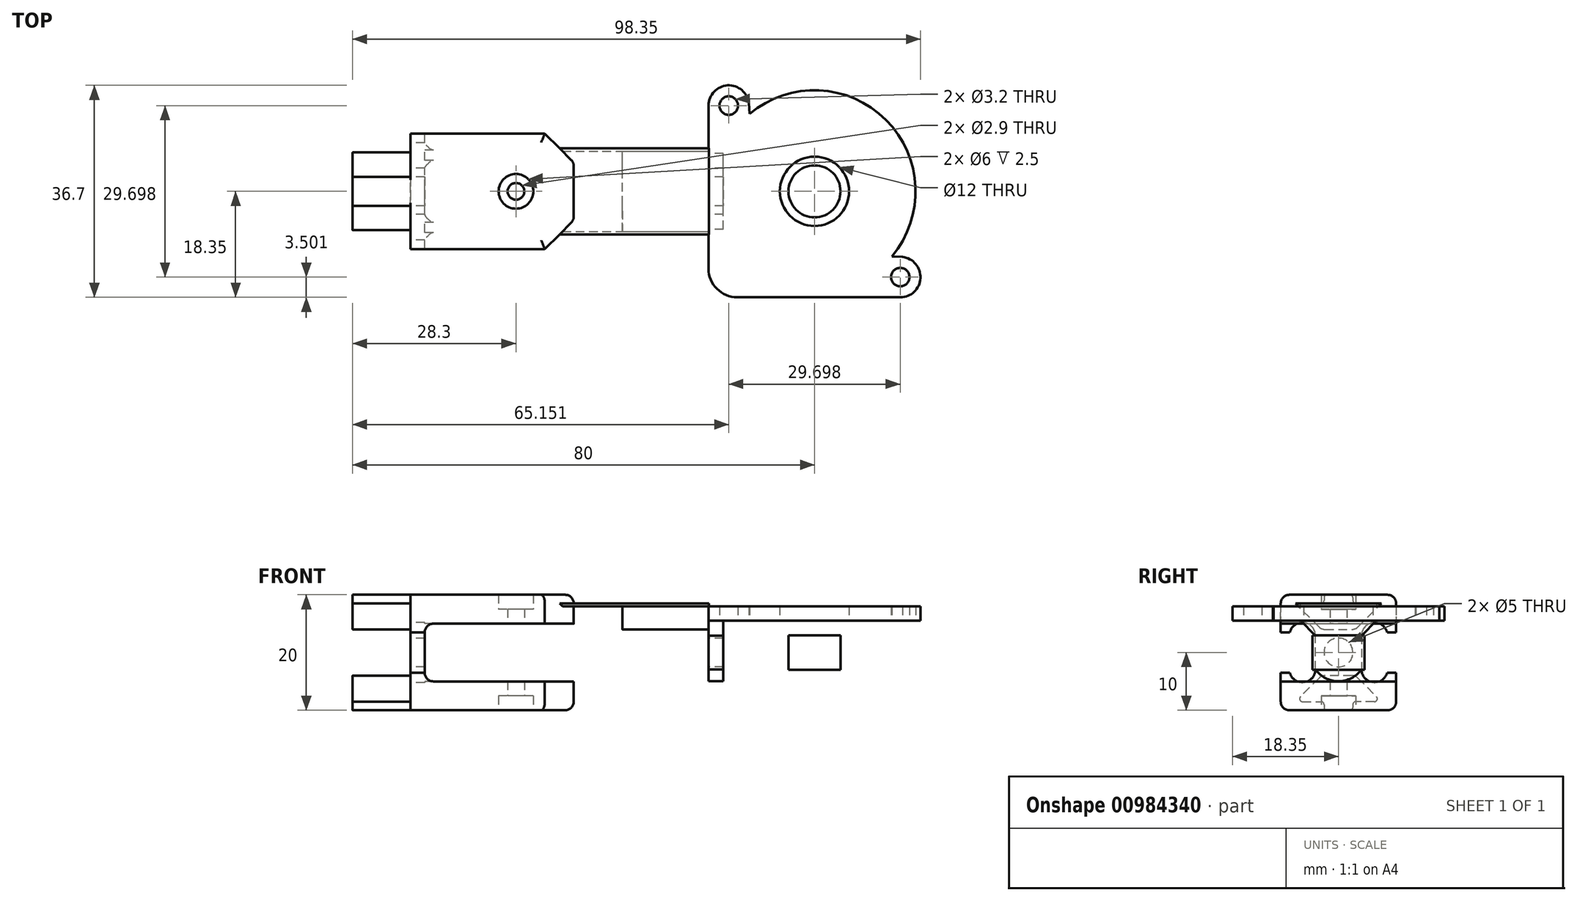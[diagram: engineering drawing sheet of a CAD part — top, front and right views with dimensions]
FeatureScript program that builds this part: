
annotation { "Feature Type Name" : "Feature", "Feature Type Description" : "" }
export const myFeature = defineFeature(function(context is Context, id is Id, definition is map)
    precondition{}
    {
        {
            var Q0;
            Q0=qCreatedBy(makeId("Top.planeOp"),FACE);
            cPlane(context, id + "F0", {"entities" : qUnion([Q0]), "cplaneType" : CPlaneType.OFFSET, "offset" : 2.5 * mm, "oppositeDirection" : true, "width" : 150 * mm, "height" : 150 * mm});
        }
        {
            var Q0;
            Q0=qCreatedBy(makeId("Right.planeOp"),FACE);
            cPlane(context, id + "F1", {"entities" : qUnion([Q0]), "cplaneType" : CPlaneType.OFFSET, "offset" : 18.3 * mm, "oppositeDirection" : true, "width" : 150 * mm, "height" : 150 * mm});
        }
        {
            var Q0;
            Q0=qCreatedBy(makeId("Right.planeOp"),FACE);
            cPlane(context, id + "F2", {"entities" : qUnion([Q0]), "cplaneType" : CPlaneType.OFFSET, "offset" : 70 * mm, "oppositeDirection" : true, "width" : 150 * mm, "height" : 150 * mm});
        }
        {
            var Q0;
            Q0=qCreatedBy(makeId("Top.planeOp"),FACE);
            cPlane(context, id + "F3", {"entities" : qUnion([Q0]), "cplaneType" : CPlaneType.OFFSET, "offset" : 5.5 * mm, "oppositeDirection" : true, "width" : 150 * mm, "height" : 150 * mm});
        }
        {
            var Q0;
            Q0=qCreatedBy(makeId("Top.planeOp"),FACE);
            var sketch = newSketch(context, id + "F4", { "sketchPlane" : qUnion([Q0])});
            skLineSegment(sketch, "E0", {"start": v(-14.85, 14.85) * mm, "end": v(14.85, -14.85) * mm, "construction": true});
            skCircle(sketch, "E1", {"center": v(14.85, -14.85) * mm, "radius": 1.6 * mm});
            skCircle(sketch, "E2", {"center": v(0, 0) * mm, "radius": 6 * mm});
            skCircle(sketch, "E3", {"center": v(-14.85, 14.85) * mm, "radius": 1.6 * mm});
            skLineSegment(sketch, "E4", {"start": v(-18.35, 14.85) * mm, "end": v(-17.47, -0.97) * mm, "construction": true});
            skLineSegment(sketch, "E5", {"start": v(-0.97, -17.47) * mm, "end": v(14.85, -18.35) * mm, "construction": true});
            skLineSegment(sketch, "E6", {"start": v(-11.26, 13.4) * mm, "end": v(-11.37, 15.24) * mm});
            skLineSegment(sketch, "E7", {"start": v(13.4, -11.26) * mm, "end": v(15.24, -11.37) * mm});
            skArc(sketch, "E8", {"start": v(-18.35, 14.85) * mm, "mid": v(-15.04, 18.35) * mm, "end": v(-11.37, 15.24) * mm});
            skArc(sketch, "E9", {"start": v(15.24, -11.37) * mm, "mid": v(18.35, -15.04) * mm, "end": v(14.85, -18.35) * mm});
            skArc(sketch, "E10", {"start": v(-17.47, -0.97) * mm, "mid": v(-12.37, -12.37) * mm, "end": v(-0.97, -17.47) * mm, "construction": true});
            skArc(sketch, "E11", {"start": v(-11.26, 13.4) * mm, "mid": v(12.37, 12.37) * mm, "end": v(13.4, -11.26) * mm});
            skLineSegment(sketch, "E12.0", {"start": v(-18.35, 14.85) * mm, "end": v(14.85, -18.35) * mm, "construction": true});
            skLineSegment(sketch, "E13.top", {"start": v(-18.35, -18.35) * mm, "end": v(14.85, -18.35) * mm});
            skLineSegment(sketch, "E13.left", {"start": v(-18.35, 14.85) * mm, "end": v(-18.35, -18.35) * mm});
            skLineSegment(sketch, "E14", {"start": v(-40.55, 25) * mm, "end": v(-40.55, -27.36) * mm, "construction": true});
            skLineSegment(sketch, "E15.MirrorCS", {"start": v(-94.5, -11.26) * mm, "end": v(-96.35, -11.37) * mm});
            skLineSegment(sketch, "E16.MirrorCS", {"start": v(-69.84, 13.4) * mm, "end": v(-69.74, 15.24) * mm});
            skArc(sketch, "E17.MirrorCS", {"start": v(-62.75, 14.85) * mm, "mid": v(-66.06, 18.35) * mm, "end": v(-69.74, 15.24) * mm});
            skArc(sketch, "E18.MirrorCS", {"start": v(-69.84, 13.4) * mm, "mid": v(-93.48, 12.37) * mm, "end": v(-94.5, -11.26) * mm});
            skCircle(sketch, "E19.MirrorC", {"center": v(-95.96, -14.85) * mm, "radius": 1.6 * mm});
            skLineSegment(sketch, "E20.MirrorCS", {"start": v(-62.75, -18.35) * mm, "end": v(-95.96, -18.35) * mm});
            skCircle(sketch, "E21.MirrorC", {"center": v(-66.26, 14.85) * mm, "radius": 1.6 * mm});
            skArc(sketch, "E22.MirrorCS", {"start": v(-96.35, -11.37) * mm, "mid": v(-99.46, -15.04) * mm, "end": v(-95.96, -18.35) * mm});
            skLineSegment(sketch, "E23.MirrorCS", {"start": v(-62.75, 14.85) * mm, "end": v(-62.75, -18.35) * mm});
            skCircle(sketch, "E24", {"center": v(-81.1, 0) * mm, "radius": 1.35 * mm});
            skSolve(sketch);
        }
        {
            var Q0;
            Q0=qCreatedBy(id+"F0.planeOp",FACE);
            var sketch = newSketch(context, id + "F5", { "sketchPlane" : qUnion([Q0])});
            skCircle(sketch, "E25", {"center": v(0, 0) * mm, "radius": 4.5 * mm});
            skSolve(sketch);
        }
        {
            var Q0;
            Q0=qCreatedBy(id+"F1.planeOp",FACE);
            var sketch = newSketch(context, id + "F6", { "sketchPlane" : qUnion([Q0])});
            skLineSegment(sketch, "E26.0", {"start": v(4, -2.56) * mm, "end": v(6.56, 0) * mm});
            skLineSegment(sketch, "E26.1", {"start": v(4, -2.56) * mm, "end": v(4, -8.44) * mm});
            skLineSegment(sketch, "E26.2", {"start": v(-4, -8.44) * mm, "end": v(-4, -2.56) * mm});
            skLineSegment(sketch, "E26.3", {"start": v(-6.56, 0) * mm, "end": v(-4, -2.56) * mm});
            skCircle(sketch, "E26.4", {"center": v(0, -5.5) * mm, "radius": 2.5 * mm});
            skCircle(sketch, "E27", {"center": v(0, 0) * mm, "radius": 2.5 * mm, "construction": true});
            skArc(sketch, "E28", {"start": v(-4, -8.44) * mm, "mid": v(0, -10.46) * mm, "end": v(4, -8.44) * mm});
            skLineSegment(sketch, "E29", {"start": v(-2.94, -1.5) * mm, "end": v(2.94, -1.5) * mm});
            skLineSegment(sketch, "E30", {"start": v(-6.56, 0) * mm, "end": v(-6.94, 2.5) * mm});
            skLineSegment(sketch, "E31", {"start": v(6.56, 0) * mm, "end": v(6.94, 2.5) * mm});
            skLineSegment(sketch, "E32", {"start": v(-6.94, 2.5) * mm, "end": v(6.94, 2.5) * mm});
            skLineSegment(sketch, "E33", {"start": v(-2.94, -1.5) * mm, "end": v(-6.94, 2.5) * mm});
            skLineSegment(sketch, "E34", {"start": v(2.94, -1.5) * mm, "end": v(6.94, 2.5) * mm});
            skLineSegment(sketch, "E35", {"start": v(-7.44, 3) * mm, "end": v(7.44, 3) * mm});
            skLineSegment(sketch, "E36", {"start": v(-7.44, 3) * mm, "end": v(-6.94, 2.5) * mm});
            skLineSegment(sketch, "E37", {"start": v(7.44, 3) * mm, "end": v(6.94, 2.5) * mm});
            skSolve(sketch);
        }
        {
            var Q0;
            Q0=qCreatedBy(id+"F2.planeOp",FACE);
            var sketch = newSketch(context, id + "F7", { "sketchPlane" : qUnion([Q0])});
            skCircle(sketch, "E38.0", {"center": v(0, -5.5) * mm, "radius": 2.5 * mm});
            skLineSegment(sketch, "E39", {"start": v(-2.5, -14) * mm, "end": v(-2.5, -15.5) * mm});
            skLineSegment(sketch, "E40", {"start": v(-10, -9) * mm, "end": v(-8.43, -9) * mm});
            skLineSegment(sketch, "E41", {"start": v(-10, -2) * mm, "end": v(-8.43, -2) * mm});
            skLineSegment(sketch, "E42", {"start": v(2.5, -14) * mm, "end": v(2.5, -15.5) * mm});
            skLineSegment(sketch, "E43", {"start": v(8.43, -9) * mm, "end": v(10, -9) * mm});
            skLineSegment(sketch, "E44", {"start": v(8.43, -2) * mm, "end": v(10, -2) * mm});
            skLineSegment(sketch, "E45", {"start": v(-2.94, -1.5) * mm, "end": v(-7.44, 3) * mm});
            skLineSegment(sketch, "E46", {"start": v(2.94, -1.5) * mm, "end": v(7.44, 3) * mm});
            skLineSegment(sketch, "E47", {"start": v(2.94, -9.5) * mm, "end": v(7.44, -14) * mm});
            skLineSegment(sketch, "E48", {"start": v(-2.94, -9.5) * mm, "end": v(-7.44, -14) * mm});
            skLineSegment(sketch, "E49", {"start": v(-2.5, 4.5) * mm, "end": v(-2.5, 3) * mm});
            skLineSegment(sketch, "E50", {"start": v(2.5, 4.5) * mm, "end": v(2.5, 3) * mm});
            skLineSegment(sketch, "E51", {"start": v(-7.44, -14) * mm, "end": v(-2.5, -14) * mm});
            skLineSegment(sketch, "E52", {"start": v(-2.5, 3) * mm, "end": v(-7.44, 3) * mm});
            skLineSegment(sketch, "E53", {"start": v(2.5, 3) * mm, "end": v(7.44, 3) * mm});
            skLineSegment(sketch, "E54", {"start": v(7.44, -14) * mm, "end": v(2.5, -14) * mm});
            skLineSegment(sketch, "E55", {"start": v(-2.94, -1.5) * mm, "end": v(2.94, -1.5) * mm});
            skLineSegment(sketch, "E56", {"start": v(4, -2.56) * mm, "end": v(4, -8.44) * mm});
            skLineSegment(sketch, "E57", {"start": v(2.94, -9.5) * mm, "end": v(-2.94, -9.5) * mm});
            skLineSegment(sketch, "E58", {"start": v(-4, -8.44) * mm, "end": v(-4, -2.56) * mm});
            skLineSegment(sketch, "E59", {"start": v(10, 4.5) * mm, "end": v(-10, 4.5) * mm});
            skLineSegment(sketch, "E60", {"start": v(10, 4.5) * mm, "end": v(10, -15.5) * mm});
            skLineSegment(sketch, "E61", {"start": v(-10, 4.5) * mm, "end": v(-10, -15.5) * mm});
            skLineSegment(sketch, "E62", {"start": v(10, -15.5) * mm, "end": v(-10, -15.5) * mm});
            skLineSegment(sketch, "E63", {"start": v(10, -5.5) * mm, "end": v(-10, -5.5) * mm, "construction": true});
            skLineSegment(sketch, "E64", {"start": v(0, 4.5) * mm, "end": v(0, -15.5) * mm, "construction": true});
            skArc(sketch, "E65", {"start": v(8.43, -2) * mm, "mid": v(5.97, -0.33) * mm, "end": v(4, -2.56) * mm});
            skArc(sketch, "E66", {"start": v(-8.43, -2) * mm, "mid": v(-5.97, -0.33) * mm, "end": v(-4, -2.56) * mm});
            skArc(sketch, "E67", {"start": v(-8.43, -9) * mm, "mid": v(-5.97, -10.67) * mm, "end": v(-4, -8.44) * mm});
            skArc(sketch, "E68", {"start": v(8.43, -9) * mm, "mid": v(5.97, -10.67) * mm, "end": v(4, -8.44) * mm});
            skSolve(sketch);
        }
        {
            var Q0;
            Q0=qCreatedBy(id+"F3.planeOp",FACE);
            var sketch = newSketch(context, id + "F8", { "sketchPlane" : qUnion([Q0])});
            skLineSegment(sketch, "E69.1", {"start": v(-67.5, -10) * mm, "end": v(-67.5, 10) * mm});
            skLineSegment(sketch, "E70", {"start": v(-41.7, -10) * mm, "end": v(-41.7, 10) * mm});
            skLineSegment(sketch, "E71", {"start": v(-67.5, -10) * mm, "end": v(-41.7, -10) * mm});
            skLineSegment(sketch, "E72", {"start": v(-67.5, 10) * mm, "end": v(-41.7, 10) * mm});
            skCircle(sketch, "E73", {"center": v(-51.7, 0) * mm, "radius": 1.45 * mm});
            skCircle(sketch, "E74", {"center": v(-51.7, 0) * mm, "radius": 5 * mm, "construction": true});
            skCircle(sketch, "E75", {"center": v(-51.7, 0) * mm, "radius": 3 * mm});
            skSolve(sketch);
        }
        {
            var Q0;
            Q0=makeQuery(id+"F4.imprint","IMPRINT",FACE,{"disambiguationData":[TD([[makeQuery(id+"F4.imprint","IMPRINT",EDGE,{"derivedFrom":sQuery(id+"F4.wireOp",EDGE,"E1")}),-1.0]])]});
            extrude(context, id + "F9", {"entities" : qUnion([Q0]), "depth" : 2.5 * mm, "offsetDistance" : 25 * mm});
        }
        {
            var Q0;
            Q0=makeQuery(id+"F5.imprint","IMPRINT",FACE,{"disambiguationData":[TD([[makeQuery(id+"F5.imprint","IMPRINT",EDGE,{"derivedFrom":sQuery(id+"F5.wireOp",EDGE,"E25")}),1.0]])]});
            extrude(context, id + "F10", {"entities" : qUnion([Q0]), "oppositeDirection" : true, "depth" : 6 * mm, "offsetDistance" : 25 * mm});
        }
        {
            var Q0;
            Q0=makeQuery(id+"F6.imprint","IMPRINT",FACE,{"disambiguationData":[TD([[makeQuery(id+"F6.imprint","IMPRINT",EDGE,{"derivedFrom":sQuery(id+"F6.wireOp",EDGE,"E26.0")}),1.0]])]});
            var Q1;
            Q1=makeQuery(id+"F6.imprint","IMPRINT",FACE,{"disambiguationData":[TD([[makeQuery(id+"F6.imprint","IMPRINT",EDGE,{"derivedFrom":sQuery(id+"F6.wireOp",EDGE,"E29")}),1.0]])]});
            extrude(context, id + "F11", {"entities" : qUnion([Q0, Q1]), "operationType" : NewBodyOperationType.ADD, "depth" : 2.5 * mm, "offsetDistance" : 25 * mm});
        }
        {
            var Q0;
            Q0=makeQuery(id+"F6.imprint","IMPRINT",FACE,{"disambiguationData":[TD([[makeQuery(id+"F6.imprint","IMPRINT",EDGE,{"derivedFrom":sQuery(id+"F6.wireOp",EDGE,"E26.0")}),1.0]])]});
            var Q1;
            Q1=makeQuery(id+"F6.imprint","IMPRINT",FACE,{"disambiguationData":[TD([[makeQuery(id+"F6.imprint","IMPRINT",EDGE,{"derivedFrom":sQuery(id+"F6.wireOp",EDGE,"E29")}),1.0]])]});
            extrude(context, id + "F12", {"entities" : qUnion([Q0, Q1]), "operationType" : NewBodyOperationType.ADD, "oppositeDirection" : true, "depth" : 0.2 * mm, "offsetDistance" : 25 * mm});
        }
        {
            var Q0;
            Q0=makeQuery(id+"F6.imprint","IMPRINT",FACE,{"disambiguationData":[TD([[makeQuery(id+"F6.imprint","IMPRINT",EDGE,{"derivedFrom":sQuery(id+"F6.wireOp",EDGE,"E29")}),1.0]])]});
            extrude(context, id + "F13", {"entities" : qUnion([Q0]), "operationType" : NewBodyOperationType.ADD, "oppositeDirection" : true, "depth" : 15 * mm, "offsetDistance" : 25 * mm});
        }
        {
            var Q0;
            Q0=makeQuery(id+"F12.opExtrude","CAP_FACE",FACE,{"disambiguationData":[OSD([sQuery(id+"F6.wireOp",EDGE,"E26.0"),sQuery(id+"F6.wireOp",EDGE,"E26.1"),sQuery(id+"F6.wireOp",EDGE,"E26.2"),sQuery(id+"F6.wireOp",EDGE,"E26.3"),sQuery(id+"F6.wireOp",EDGE,"E26.4"),sQuery(id+"F6.wireOp",EDGE,"E28"),sQuery(id+"F6.wireOp",EDGE,"E30"),sQuery(id+"F6.wireOp",EDGE,"E31"),sQuery(id+"F6.wireOp",EDGE,"E32")])],"isStart":false});
            var Q1;
            {var subQ0=sQuery(id+"F4.wireOp",EDGE,"E13.top");var subQ2=sQuery(id+"F4.wireOp",EDGE,"E13.left");Q1=makeQuery(id+"F12.boolean.opBoolean","SPLIT",FACE,{"disambiguationData":[TD([makeQuery(id+"F9.opExtrude","SWEPT_FACE",FACE,{"disambiguationData":[OSD([subQ0])]})])],"derivedFrom":makeQuery(id+"F9.opExtrude","SWEPT_FACE",FACE,{"disambiguationData":[OSD([subQ2])]})});}
            extrude(context, id + "F14", {"entities" : qUnion([Q0]), "operationType" : NewBodyOperationType.REMOVE, "endBound" : BoundingType.UP_TO_SURFACE, "oppositeDirection" : true, "depth" : 25 * mm, "endBoundEntityFace" : qUnion([Q1]), "offsetDistance" : 25 * mm});
        }
        {
            var Q0;
            Q0=makeQuery(id+"F6.imprint","IMPRINT",FACE,{"disambiguationData":[TD([[makeQuery(id+"F6.imprint","IMPRINT",EDGE,{"derivedFrom":sQuery(id+"F6.wireOp",EDGE,"E32")}),1.0]])]});
            extrude(context, id + "F15", {"entities" : qUnion([Q0]), "oppositeDirection" : true, "depth" : 25 * mm, "offsetDistance" : 25 * mm});
        }
        {
            var Q0;
            Q0=makeQuery(id+"F7.imprint","IMPRINT",FACE,{"disambiguationData":[TD([[makeQuery(id+"F7.imprint","IMPRINT",EDGE,{"derivedFrom":sQuery(id+"F7.wireOp",EDGE,"E38.0")}),-1.0]])]});
            var Q1;
            Q1=makeQuery(id+"F7.imprint","IMPRINT",FACE,{"disambiguationData":[TD([[makeQuery(id+"F7.imprint","IMPRINT",EDGE,{"derivedFrom":sQuery(id+"F7.wireOp",EDGE,"E45")}),-1.0]])]});
            var Q2;
            {var subQ1=sQuery(id+"F7.wireOp",EDGE,"E39");Q2=makeQuery(id+"F7.imprint","IMPRINT",FACE,{"disambiguationData":[TD([[makeQuery(id+"F7.imprint","IMPRINT",EDGE,{"derivedFrom":subQ1}),1.0]])]});}
            extrude(context, id + "F16", {"entities" : qUnion([Q0, Q1, Q2]), "depth" : 2.5 * mm, "offsetDistance" : 25 * mm});
        }
        {
            var Q0;
            Q0=makeQuery(id+"F7.imprint","IMPRINT",FACE,{"disambiguationData":[TD([[makeQuery(id+"F7.imprint","IMPRINT",EDGE,{"derivedFrom":sQuery(id+"F7.wireOp",EDGE,"E45")}),-1.0]])]});
            var Q1;
            {var subQ1=sQuery(id+"F7.wireOp",EDGE,"E39");Q1=makeQuery(id+"F7.imprint","IMPRINT",FACE,{"disambiguationData":[TD([[makeQuery(id+"F7.imprint","IMPRINT",EDGE,{"derivedFrom":subQ1}),1.0]])]});}
            extrude(context, id + "F17", {"entities" : qUnion([Q0, Q1]), "operationType" : NewBodyOperationType.ADD, "oppositeDirection" : true, "depth" : 10 * mm, "offsetDistance" : 25 * mm});
        }
        {
            var Q0;
            Q0=makeQuery(id+"F8.imprint","IMPRINT",FACE,{"disambiguationData":[TD([[makeQuery(id+"F8.imprint","IMPRINT",EDGE,{"derivedFrom":sQuery(id+"F8.wireOp",EDGE,"E69.1")}),-1.0]])]});
            extrude(context, id + "F18", {"entities" : qUnion([Q0]), "operationType" : NewBodyOperationType.ADD, "depth" : 20 * mm, "offsetDistance" : 25 * mm, "symmetric" : true});
        }
        {
            var Q0;
            Q0=makeQuery(id+"F8.imprint","IMPRINT",FACE,{"disambiguationData":[TD([[makeQuery(id+"F8.imprint","IMPRINT",EDGE,{"derivedFrom":sQuery(id+"F8.wireOp",EDGE,"E73")}),-1.0]])]});
            extrude(context, id + "F19", {"entities" : qUnion([Q0]), "operationType" : NewBodyOperationType.ADD, "depth" : 15 * mm, "offsetDistance" : 25 * mm, "symmetric" : true});
        }
        {
            var Q0;
            Q0=makeQuery(id+"F8.imprint","IMPRINT",FACE,{"disambiguationData":[TD([[makeQuery(id+"F8.imprint","IMPRINT",EDGE,{"derivedFrom":sQuery(id+"F8.wireOp",EDGE,"E69.1")}),-1.0]])]});
            var Q1;
            Q1=makeQuery(id+"F8.imprint","IMPRINT",FACE,{"disambiguationData":[TD([[makeQuery(id+"F8.imprint","IMPRINT",EDGE,{"derivedFrom":sQuery(id+"F8.wireOp",EDGE,"E73")}),-1.0]])]});
            extrude(context, id + "F20", {"entities" : qUnion([Q0, Q1]), "operationType" : NewBodyOperationType.REMOVE, "depth" : 10 * mm, "offsetDistance" : 25 * mm, "symmetric" : true});
        }
        {
            var Q0;
            {var subQ0=sQuery(id+"F7.wireOp",EDGE,"E62");var subQ3=sQuery(id+"F8.wireOp",EDGE,"E71");var subQ4=sQuery(id+"F8.wireOp",EDGE,"E70");Q0=makeQuery(id+"F20.boolean.opBoolean","SPLIT",EDGE,{"disambiguationData":[TD([makeQuery(id+"F16.opExtrude","SWEPT_FACE",FACE,{"disambiguationData":[OSD([subQ0])]})])],"derivedFrom":makeQuery(id+"F18.opExtrude","SWEPT_EDGE",EDGE,{"disambiguationData":[OSD([subQ4,subQ3])]})});}
            var Q1;
            {var subQ0=sQuery(id+"F7.wireOp",EDGE,"E62");var subQ2=sQuery(id+"F8.wireOp",EDGE,"E72");var subQ4=sQuery(id+"F8.wireOp",EDGE,"E70");Q1=makeQuery(id+"F20.boolean.opBoolean","SPLIT",EDGE,{"disambiguationData":[TD([makeQuery(id+"F16.opExtrude","SWEPT_FACE",FACE,{"disambiguationData":[OSD([subQ0])]})])],"derivedFrom":makeQuery(id+"F18.opExtrude","SWEPT_EDGE",EDGE,{"disambiguationData":[OSD([subQ4,subQ2])]})});}
            var Q2;
            {var subQ1=sQuery(id+"F7.wireOp",EDGE,"E59");var subQ3=sQuery(id+"F8.wireOp",EDGE,"E71");var subQ4=sQuery(id+"F8.wireOp",EDGE,"E70");Q2=makeQuery(id+"F20.boolean.opBoolean","SPLIT",EDGE,{"disambiguationData":[TD([makeQuery(id+"F16.opExtrude","SWEPT_FACE",FACE,{"disambiguationData":[OSD([subQ1])]})])],"derivedFrom":makeQuery(id+"F18.opExtrude","SWEPT_EDGE",EDGE,{"disambiguationData":[OSD([subQ4,subQ3])]})});}
            var Q3;
            {var subQ1=sQuery(id+"F7.wireOp",EDGE,"E59");var subQ2=sQuery(id+"F8.wireOp",EDGE,"E72");var subQ4=sQuery(id+"F8.wireOp",EDGE,"E70");Q3=makeQuery(id+"F20.boolean.opBoolean","SPLIT",EDGE,{"disambiguationData":[TD([makeQuery(id+"F16.opExtrude","SWEPT_FACE",FACE,{"disambiguationData":[OSD([subQ1])]})])],"derivedFrom":makeQuery(id+"F18.opExtrude","SWEPT_EDGE",EDGE,{"disambiguationData":[OSD([subQ4,subQ2])]})});}
            chamfer(context, id + "F21", {"entities" : qUnion([Q0, Q1, Q2, Q3]), "width" : 5 * mm, "tangentPropagation" : true});
        }
        {
            var Q0;
            {var subQ0=sQuery(id+"F6.wireOp",EDGE,"E33");var subQ1=sQuery(id+"F6.wireOp",EDGE,"E29");Q0=makeQuery(id+"F14.boolean.opBoolean","MERGE",EDGE,{"derivedFrom":[makeQuery(id+"F13.opExtrude","SWEPT_EDGE",EDGE,{"disambiguationData":[OSD([subQ1,subQ0])]})],"fromTools":[makeQuery(id+"F14.opExtrude","SWEPT_EDGE",EDGE,{"disambiguationData":[OSD([sQuery(id+"F6.wireOp",EDGE,"E26.0"),sQuery(id+"F6.wireOp",EDGE,"E26.1"),sQuery(id+"F6.wireOp",EDGE,"E26.2"),sQuery(id+"F6.wireOp",EDGE,"E26.3"),sQuery(id+"F6.wireOp",EDGE,"E26.4"),sQuery(id+"F6.wireOp",EDGE,"E28"),subQ1,sQuery(id+"F6.wireOp",EDGE,"E30"),sQuery(id+"F6.wireOp",EDGE,"E31"),sQuery(id+"F6.wireOp",EDGE,"E32"),subQ0])]})]});}
            var Q1;
            {var subQ0=sQuery(id+"F6.wireOp",EDGE,"E34");var subQ1=sQuery(id+"F6.wireOp",EDGE,"E29");Q1=makeQuery(id+"F14.boolean.opBoolean","MERGE",EDGE,{"derivedFrom":[makeQuery(id+"F13.opExtrude","SWEPT_EDGE",EDGE,{"disambiguationData":[OSD([subQ1,subQ0])]})],"fromTools":[makeQuery(id+"F14.opExtrude","SWEPT_EDGE",EDGE,{"disambiguationData":[OSD([sQuery(id+"F6.wireOp",EDGE,"E26.0"),sQuery(id+"F6.wireOp",EDGE,"E26.1"),sQuery(id+"F6.wireOp",EDGE,"E26.2"),sQuery(id+"F6.wireOp",EDGE,"E26.3"),sQuery(id+"F6.wireOp",EDGE,"E26.4"),sQuery(id+"F6.wireOp",EDGE,"E28"),subQ1,sQuery(id+"F6.wireOp",EDGE,"E30"),sQuery(id+"F6.wireOp",EDGE,"E31"),sQuery(id+"F6.wireOp",EDGE,"E32"),subQ0])]})]});}
            var Q2;
            Q2=makeQuery(id+"F17.opExtrude","SWEPT_EDGE",EDGE,{"disambiguationData":[OSD([sQuery(id+"F7.wireOp",EDGE,"E46"),sQuery(id+"F7.wireOp",EDGE,"E55")])]});
            var Q3;
            Q3=makeQuery(id+"F17.opExtrude","SWEPT_EDGE",EDGE,{"disambiguationData":[OSD([sQuery(id+"F7.wireOp",EDGE,"E45"),sQuery(id+"F7.wireOp",EDGE,"E55")])]});
            var Q4;
            Q4=makeQuery(id+"F17.opExtrude","SWEPT_EDGE",EDGE,{"disambiguationData":[OSD([sQuery(id+"F7.wireOp",EDGE,"E47"),sQuery(id+"F7.wireOp",EDGE,"E57")])]});
            var Q5;
            Q5=makeQuery(id+"F17.opExtrude","SWEPT_EDGE",EDGE,{"disambiguationData":[OSD([sQuery(id+"F7.wireOp",EDGE,"E48"),sQuery(id+"F7.wireOp",EDGE,"E57")])]});
            var Q6;
            Q6=makeQuery(id+"F16.opExtrude","SWEPT_EDGE",EDGE,{"disambiguationData":[OSD([sQuery(id+"F7.wireOp",EDGE,"E59"),sQuery(id+"F7.wireOp",EDGE,"E60")])]});
            var Q7;
            Q7=makeQuery(id+"F16.opExtrude","SWEPT_EDGE",EDGE,{"disambiguationData":[OSD([sQuery(id+"F7.wireOp",EDGE,"E60"),sQuery(id+"F7.wireOp",EDGE,"E62")])]});
            var Q8;
            Q8=makeQuery(id+"F16.opExtrude","SWEPT_EDGE",EDGE,{"disambiguationData":[OSD([sQuery(id+"F7.wireOp",EDGE,"E61"),sQuery(id+"F7.wireOp",EDGE,"E62")])]});
            var Q9;
            Q9=makeQuery(id+"F16.opExtrude","SWEPT_EDGE",EDGE,{"disambiguationData":[OSD([sQuery(id+"F7.wireOp",EDGE,"E59"),sQuery(id+"F7.wireOp",EDGE,"E61")])]});
            var Q10;
            {var subQ1=sQuery(id+"F7.wireOp",EDGE,"E62");var subQ4=sQuery(id+"F8.wireOp",EDGE,"E71");var subQ5=sQuery(id+"F8.wireOp",EDGE,"E70");var subQ12=makeQuery(id+"F16.opExtrude","SWEPT_FACE",FACE,{"disambiguationData":[OSD([subQ1])]});var subQ15=makeQuery(id+"F18.opExtrude","SWEPT_FACE",FACE,{"disambiguationData":[OSD([subQ5])]});Q10=makeQuery(id+"F21.opChamfer","BLEND_EDGE",EDGE,{"blendedFrom":[makeQuery(id+"F20.boolean.opBoolean","SPLIT",EDGE,{"disambiguationData":[TD([subQ12])],"derivedFrom":makeQuery(id+"F18.opExtrude","SWEPT_EDGE",EDGE,{"disambiguationData":[OSD([subQ5,subQ4])]})}),makeQuery(id+"F20.boolean.opBoolean","SPLIT",FACE,{"disambiguationData":[TD([subQ12])],"derivedFrom":subQ15})],"blendedInto":[makeQuery(id+"F20.boolean.opBoolean","SPLIT",FACE,{"disambiguationData":[TD([subQ12])],"derivedFrom":subQ15})]});}
            var Q11;
            {var subQ1=sQuery(id+"F7.wireOp",EDGE,"E62");var subQ2=sQuery(id+"F8.wireOp",EDGE,"E72");var subQ4=sQuery(id+"F8.wireOp",EDGE,"E70");var subQ12=makeQuery(id+"F16.opExtrude","SWEPT_FACE",FACE,{"disambiguationData":[OSD([subQ1])]});var subQ15=makeQuery(id+"F18.opExtrude","SWEPT_FACE",FACE,{"disambiguationData":[OSD([subQ4])]});Q11=makeQuery(id+"F21.opChamfer","BLEND_EDGE",EDGE,{"blendedFrom":[makeQuery(id+"F20.boolean.opBoolean","SPLIT",EDGE,{"disambiguationData":[TD([subQ12])],"derivedFrom":makeQuery(id+"F18.opExtrude","SWEPT_EDGE",EDGE,{"disambiguationData":[OSD([subQ4,subQ2])]})}),makeQuery(id+"F20.boolean.opBoolean","SPLIT",FACE,{"disambiguationData":[TD([subQ12])],"derivedFrom":subQ15})],"blendedInto":[makeQuery(id+"F20.boolean.opBoolean","SPLIT",FACE,{"disambiguationData":[TD([subQ12])],"derivedFrom":subQ15})]});}
            var Q12;
            {var subQ1=sQuery(id+"F7.wireOp",EDGE,"E59");var subQ6=makeQuery(id+"F16.opExtrude","SWEPT_FACE",FACE,{"disambiguationData":[OSD([subQ1])]});var subQ9=sQuery(id+"F8.wireOp",EDGE,"E71");var subQ10=sQuery(id+"F8.wireOp",EDGE,"E70");var subQ15=makeQuery(id+"F18.opExtrude","SWEPT_FACE",FACE,{"disambiguationData":[OSD([subQ10])]});Q12=makeQuery(id+"F21.opChamfer","BLEND_EDGE",EDGE,{"blendedFrom":[makeQuery(id+"F20.boolean.opBoolean","SPLIT",EDGE,{"disambiguationData":[TD([subQ6])],"derivedFrom":makeQuery(id+"F18.opExtrude","SWEPT_EDGE",EDGE,{"disambiguationData":[OSD([subQ10,subQ9])]})}),makeQuery(id+"F20.boolean.opBoolean","SPLIT",FACE,{"disambiguationData":[TD([subQ6])],"derivedFrom":subQ15})],"blendedInto":[makeQuery(id+"F20.boolean.opBoolean","SPLIT",FACE,{"disambiguationData":[TD([subQ6])],"derivedFrom":subQ15})]});}
            var Q13;
            {var subQ1=sQuery(id+"F7.wireOp",EDGE,"E59");var subQ7=makeQuery(id+"F16.opExtrude","SWEPT_FACE",FACE,{"disambiguationData":[OSD([subQ1])]});var subQ8=sQuery(id+"F8.wireOp",EDGE,"E72");var subQ10=sQuery(id+"F8.wireOp",EDGE,"E70");var subQ15=makeQuery(id+"F18.opExtrude","SWEPT_FACE",FACE,{"disambiguationData":[OSD([subQ10])]});Q13=makeQuery(id+"F21.opChamfer","BLEND_EDGE",EDGE,{"blendedFrom":[makeQuery(id+"F20.boolean.opBoolean","SPLIT",EDGE,{"disambiguationData":[TD([subQ7])],"derivedFrom":makeQuery(id+"F18.opExtrude","SWEPT_EDGE",EDGE,{"disambiguationData":[OSD([subQ10,subQ8])]})}),makeQuery(id+"F20.boolean.opBoolean","SPLIT",FACE,{"disambiguationData":[TD([subQ7])],"derivedFrom":subQ15})],"blendedInto":[makeQuery(id+"F20.boolean.opBoolean","SPLIT",FACE,{"disambiguationData":[TD([subQ7])],"derivedFrom":subQ15})]});}
            var Q14;
            {var subQ0=sQuery(id+"F8.wireOp",EDGE,"E69.1");var subQ1=makeQuery(id+"F20.opExtrude","SWEPT_FACE",FACE,{"disambiguationData":[OSD([subQ0])]});var subQ2=makeQuery(id+"F20.opExtrude","CAP_FACE",FACE,{"disambiguationData":[OSD([subQ0,sQuery(id+"F8.wireOp",EDGE,"E70"),sQuery(id+"F8.wireOp",EDGE,"E71"),sQuery(id+"F8.wireOp",EDGE,"E72"),sQuery(id+"F8.wireOp",EDGE,"E73")])],"isStart":false});Q14=makeQuery(id+"F20.boolean.opBoolean","COPY",EDGE,{"disambiguationData":[topologyDisambiguationEdgeConnected([subQ1,subQ2]),TD([makeQuery(id+"F16.opExtrude","SWEPT_FACE",FACE,{"disambiguationData":[OSD([sQuery(id+"F7.wireOp",EDGE,"E65")])]}),makeQuery(id+"F16.opExtrude","SWEPT_FACE",FACE,{"disambiguationData":[OSD([sQuery(id+"F7.wireOp",EDGE,"E66")])]}),makeQuery(id+"F18.opExtrude","SWEPT_FACE",FACE,{"disambiguationData":[OSD([subQ0])]}),subQ1,subQ2])],"derivedFrom":makeQuery(id+"F20.opExtrude","CAP_EDGE",EDGE,{"disambiguationData":[OSD([subQ0])],"isStart":false})});}
            var Q15;
            {var subQ0=sQuery(id+"F8.wireOp",EDGE,"E69.1");var subQ1=makeQuery(id+"F20.opExtrude","CAP_FACE",FACE,{"disambiguationData":[OSD([subQ0,sQuery(id+"F8.wireOp",EDGE,"E70"),sQuery(id+"F8.wireOp",EDGE,"E71"),sQuery(id+"F8.wireOp",EDGE,"E72"),sQuery(id+"F8.wireOp",EDGE,"E73")])],"isStart":true});var subQ2=makeQuery(id+"F20.opExtrude","SWEPT_FACE",FACE,{"disambiguationData":[OSD([subQ0])]});Q15=makeQuery(id+"F20.boolean.opBoolean","COPY",EDGE,{"disambiguationData":[topologyDisambiguationEdgeConnected([subQ2,subQ1]),TD([makeQuery(id+"F16.opExtrude","SWEPT_FACE",FACE,{"disambiguationData":[OSD([sQuery(id+"F7.wireOp",EDGE,"E67")])]}),makeQuery(id+"F16.opExtrude","SWEPT_FACE",FACE,{"disambiguationData":[OSD([sQuery(id+"F7.wireOp",EDGE,"E68")])]}),makeQuery(id+"F18.opExtrude","SWEPT_FACE",FACE,{"disambiguationData":[OSD([subQ0])]}),subQ2,subQ1])],"derivedFrom":makeQuery(id+"F20.opExtrude","CAP_EDGE",EDGE,{"disambiguationData":[OSD([subQ0])],"isStart":true})});}
            var Q16;
            {var subQ0=sQuery(id+"F8.wireOp",EDGE,"E69.1");var subQ1=sQuery(id+"F7.wireOp",EDGE,"E61");var subQ2=makeQuery(id+"F20.opExtrude","SWEPT_FACE",FACE,{"disambiguationData":[OSD([subQ0])]});var subQ3=sQuery(id+"F8.wireOp",EDGE,"E71");var subQ4=makeQuery(id+"F20.opExtrude","CAP_FACE",FACE,{"disambiguationData":[OSD([subQ0,sQuery(id+"F8.wireOp",EDGE,"E70"),subQ3,sQuery(id+"F8.wireOp",EDGE,"E72"),sQuery(id+"F8.wireOp",EDGE,"E73")])],"isStart":true});Q16=makeQuery(id+"F20.boolean.opBoolean","COPY",EDGE,{"disambiguationData":[topologyDisambiguationEdgeConnected([subQ2,subQ4]),TD([makeQuery(id+"F16.opExtrude","SWEPT_FACE",FACE,{"disambiguationData":[OSD([subQ1]),TDD([makeQuery(id+"F7.imprint","IMPRINT",EDGE,{"disambiguationData":[TD([[makeQuery(id+"F7.imprint","INTERSECT",VERTEX,{"derivedFrom":[sQuery(id+"F7.wireOp",EDGE,"E41"),subQ1]}),1.0]])],"derivedFrom":subQ1})])]}),makeQuery(id+"F16.opExtrude","SWEPT_FACE",FACE,{"disambiguationData":[OSD([subQ1]),TDD([makeQuery(id+"F7.imprint","IMPRINT",EDGE,{"disambiguationData":[TD([[makeQuery(id+"F7.imprint","INTERSECT",VERTEX,{"derivedFrom":[sQuery(id+"F7.wireOp",EDGE,"E40"),subQ1]}),-1.0]])],"derivedFrom":subQ1})])]}),makeQuery(id+"F16.opExtrude","SWEPT_FACE",FACE,{"disambiguationData":[OSD([sQuery(id+"F7.wireOp",EDGE,"E67")])]}),makeQuery(id+"F18.opExtrude","SWEPT_FACE",FACE,{"disambiguationData":[OSD([subQ0])]}),makeQuery(id+"F18.opExtrude","SWEPT_FACE",FACE,{"disambiguationData":[OSD([subQ3])]}),subQ2,subQ4])],"derivedFrom":makeQuery(id+"F20.opExtrude","CAP_EDGE",EDGE,{"disambiguationData":[OSD([subQ0])],"isStart":true})});}
            var Q17;
            {var subQ0=sQuery(id+"F8.wireOp",EDGE,"E71");var subQ1=sQuery(id+"F8.wireOp",EDGE,"E69.1");var subQ2=sQuery(id+"F7.wireOp",EDGE,"E61");var subQ3=makeQuery(id+"F20.opExtrude","SWEPT_FACE",FACE,{"disambiguationData":[OSD([subQ1])]});var subQ4=makeQuery(id+"F20.opExtrude","CAP_FACE",FACE,{"disambiguationData":[OSD([subQ1,sQuery(id+"F8.wireOp",EDGE,"E70"),subQ0,sQuery(id+"F8.wireOp",EDGE,"E72"),sQuery(id+"F8.wireOp",EDGE,"E73")])],"isStart":false});Q17=makeQuery(id+"F20.boolean.opBoolean","COPY",EDGE,{"disambiguationData":[topologyDisambiguationEdgeConnected([subQ3,subQ4]),TD([makeQuery(id+"F16.opExtrude","SWEPT_FACE",FACE,{"disambiguationData":[OSD([subQ2]),TDD([makeQuery(id+"F7.imprint","IMPRINT",EDGE,{"disambiguationData":[TD([[makeQuery(id+"F7.imprint","INTERSECT",VERTEX,{"derivedFrom":[sQuery(id+"F7.wireOp",EDGE,"E41"),subQ2]}),1.0]])],"derivedFrom":subQ2})])]}),makeQuery(id+"F16.opExtrude","SWEPT_FACE",FACE,{"disambiguationData":[OSD([subQ2]),TDD([makeQuery(id+"F7.imprint","IMPRINT",EDGE,{"disambiguationData":[TD([[makeQuery(id+"F7.imprint","INTERSECT",VERTEX,{"derivedFrom":[sQuery(id+"F7.wireOp",EDGE,"E40"),subQ2]}),-1.0]])],"derivedFrom":subQ2})])]}),makeQuery(id+"F16.opExtrude","SWEPT_FACE",FACE,{"disambiguationData":[OSD([sQuery(id+"F7.wireOp",EDGE,"E66")])]}),makeQuery(id+"F18.opExtrude","SWEPT_FACE",FACE,{"disambiguationData":[OSD([subQ1])]}),makeQuery(id+"F18.opExtrude","SWEPT_FACE",FACE,{"disambiguationData":[OSD([subQ0])]}),subQ3,subQ4])],"derivedFrom":makeQuery(id+"F20.opExtrude","CAP_EDGE",EDGE,{"disambiguationData":[OSD([subQ1])],"isStart":false})});}
            var Q18;
            {var subQ0=sQuery(id+"F8.wireOp",EDGE,"E69.1");var subQ1=sQuery(id+"F7.wireOp",EDGE,"E60");var subQ2=sQuery(id+"F8.wireOp",EDGE,"E72");var subQ3=makeQuery(id+"F20.opExtrude","SWEPT_FACE",FACE,{"disambiguationData":[OSD([subQ0])]});var subQ4=makeQuery(id+"F20.opExtrude","CAP_FACE",FACE,{"disambiguationData":[OSD([subQ0,sQuery(id+"F8.wireOp",EDGE,"E70"),sQuery(id+"F8.wireOp",EDGE,"E71"),subQ2,sQuery(id+"F8.wireOp",EDGE,"E73")])],"isStart":false});Q18=makeQuery(id+"F20.boolean.opBoolean","COPY",EDGE,{"disambiguationData":[topologyDisambiguationEdgeConnected([subQ3,subQ4]),TD([makeQuery(id+"F16.opExtrude","SWEPT_FACE",FACE,{"disambiguationData":[OSD([subQ1]),TDD([makeQuery(id+"F7.imprint","IMPRINT",EDGE,{"disambiguationData":[TD([[makeQuery(id+"F7.imprint","INTERSECT",VERTEX,{"derivedFrom":[sQuery(id+"F7.wireOp",EDGE,"E44"),subQ1]}),1.0]])],"derivedFrom":subQ1})])]}),makeQuery(id+"F16.opExtrude","SWEPT_FACE",FACE,{"disambiguationData":[OSD([subQ1]),TDD([makeQuery(id+"F7.imprint","IMPRINT",EDGE,{"disambiguationData":[TD([[makeQuery(id+"F7.imprint","INTERSECT",VERTEX,{"derivedFrom":[sQuery(id+"F7.wireOp",EDGE,"E43"),subQ1]}),-1.0]])],"derivedFrom":subQ1})])]}),makeQuery(id+"F16.opExtrude","SWEPT_FACE",FACE,{"disambiguationData":[OSD([sQuery(id+"F7.wireOp",EDGE,"E65")])]}),makeQuery(id+"F18.opExtrude","SWEPT_FACE",FACE,{"disambiguationData":[OSD([subQ0])]}),makeQuery(id+"F18.opExtrude","SWEPT_FACE",FACE,{"disambiguationData":[OSD([subQ2])]}),subQ3,subQ4])],"derivedFrom":makeQuery(id+"F20.opExtrude","CAP_EDGE",EDGE,{"disambiguationData":[OSD([subQ0])],"isStart":false})});}
            var Q19;
            {var subQ0=sQuery(id+"F8.wireOp",EDGE,"E69.1");var subQ1=sQuery(id+"F8.wireOp",EDGE,"E72");var subQ2=makeQuery(id+"F20.opExtrude","CAP_FACE",FACE,{"disambiguationData":[OSD([subQ0,sQuery(id+"F8.wireOp",EDGE,"E70"),sQuery(id+"F8.wireOp",EDGE,"E71"),subQ1,sQuery(id+"F8.wireOp",EDGE,"E73")])],"isStart":true});var subQ3=sQuery(id+"F7.wireOp",EDGE,"E60");var subQ4=makeQuery(id+"F20.opExtrude","SWEPT_FACE",FACE,{"disambiguationData":[OSD([subQ0])]});Q19=makeQuery(id+"F20.boolean.opBoolean","COPY",EDGE,{"disambiguationData":[topologyDisambiguationEdgeConnected([subQ4,subQ2]),TD([makeQuery(id+"F16.opExtrude","SWEPT_FACE",FACE,{"disambiguationData":[OSD([subQ3]),TDD([makeQuery(id+"F7.imprint","IMPRINT",EDGE,{"disambiguationData":[TD([[makeQuery(id+"F7.imprint","INTERSECT",VERTEX,{"derivedFrom":[sQuery(id+"F7.wireOp",EDGE,"E44"),subQ3]}),1.0]])],"derivedFrom":subQ3})])]}),makeQuery(id+"F16.opExtrude","SWEPT_FACE",FACE,{"disambiguationData":[OSD([subQ3]),TDD([makeQuery(id+"F7.imprint","IMPRINT",EDGE,{"disambiguationData":[TD([[makeQuery(id+"F7.imprint","INTERSECT",VERTEX,{"derivedFrom":[sQuery(id+"F7.wireOp",EDGE,"E43"),subQ3]}),-1.0]])],"derivedFrom":subQ3})])]}),makeQuery(id+"F16.opExtrude","SWEPT_FACE",FACE,{"disambiguationData":[OSD([sQuery(id+"F7.wireOp",EDGE,"E68")])]}),makeQuery(id+"F18.opExtrude","SWEPT_FACE",FACE,{"disambiguationData":[OSD([subQ0])]}),makeQuery(id+"F18.opExtrude","SWEPT_FACE",FACE,{"disambiguationData":[OSD([subQ1])]}),subQ4,subQ2])],"derivedFrom":makeQuery(id+"F20.opExtrude","CAP_EDGE",EDGE,{"disambiguationData":[OSD([subQ0])],"isStart":true})});}
            var Q20;
            {var subQ0=sQuery(id+"F8.wireOp",EDGE,"E72");var subQ1=sQuery(id+"F8.wireOp",EDGE,"E71");var subQ2=sQuery(id+"F8.wireOp",EDGE,"E70");var subQ3=sQuery(id+"F8.wireOp",EDGE,"E69.1");var subQ4=makeQuery(id+"F18.opExtrude","CAP_FACE",FACE,{"disambiguationData":[OSD([subQ3,subQ2,subQ1,subQ0,sQuery(id+"F8.wireOp",EDGE,"E75")])],"isStart":true});var subQ5=sQuery(id+"F7.wireOp",EDGE,"E62");var subQ6=makeQuery(id+"F17.opExtrude","SWEPT_FACE",FACE,{"disambiguationData":[OSD([subQ5])]});var subQ7=makeQuery(id+"F16.opExtrude","SWEPT_FACE",FACE,{"disambiguationData":[OSD([subQ5])]});Q20=makeQuery(id+"F21.opChamfer","BLEND_EDGE",EDGE,{"blendedFrom":[makeQuery(id+"F20.boolean.opBoolean","SPLIT",EDGE,{"disambiguationData":[TD([subQ7])],"derivedFrom":makeQuery(id+"F18.opExtrude","SWEPT_EDGE",EDGE,{"disambiguationData":[OSD([subQ2,subQ0])]})}),makeQuery(id+"F18.boolean.opBoolean","MERGE",FACE,{"derivedFrom":[makeQuery(id+"F17.boolean.opBoolean","MERGE",FACE,{"derivedFrom":[subQ7,subQ6]}),subQ4]})],"blendedInto":[makeQuery(id+"F18.boolean.opBoolean","MERGE",FACE,{"derivedFrom":[makeQuery(id+"F17.boolean.opBoolean","MERGE",FACE,{"derivedFrom":[subQ7,subQ6]}),subQ4]})]});}
            var Q21;
            Q21=makeQuery(id+"F18.opExtrude","CAP_EDGE",EDGE,{"disambiguationData":[OSD([sQuery(id+"F8.wireOp",EDGE,"E70")])],"isStart":true});
            var Q22;
            {var subQ0=sQuery(id+"F8.wireOp",EDGE,"E72");var subQ1=sQuery(id+"F8.wireOp",EDGE,"E71");var subQ2=sQuery(id+"F8.wireOp",EDGE,"E70");var subQ3=sQuery(id+"F8.wireOp",EDGE,"E69.1");var subQ4=makeQuery(id+"F18.opExtrude","CAP_FACE",FACE,{"disambiguationData":[OSD([subQ3,subQ2,subQ1,subQ0,sQuery(id+"F8.wireOp",EDGE,"E75")])],"isStart":true});var subQ5=sQuery(id+"F7.wireOp",EDGE,"E62");var subQ6=makeQuery(id+"F17.opExtrude","SWEPT_FACE",FACE,{"disambiguationData":[OSD([subQ5])]});var subQ7=makeQuery(id+"F16.opExtrude","SWEPT_FACE",FACE,{"disambiguationData":[OSD([subQ5])]});Q22=makeQuery(id+"F21.opChamfer","BLEND_EDGE",EDGE,{"blendedFrom":[makeQuery(id+"F20.boolean.opBoolean","SPLIT",EDGE,{"disambiguationData":[TD([subQ7])],"derivedFrom":makeQuery(id+"F18.opExtrude","SWEPT_EDGE",EDGE,{"disambiguationData":[OSD([subQ2,subQ1])]})}),makeQuery(id+"F18.boolean.opBoolean","MERGE",FACE,{"derivedFrom":[makeQuery(id+"F17.boolean.opBoolean","MERGE",FACE,{"derivedFrom":[subQ7,subQ6]}),subQ4]})],"blendedInto":[makeQuery(id+"F18.boolean.opBoolean","MERGE",FACE,{"derivedFrom":[makeQuery(id+"F17.boolean.opBoolean","MERGE",FACE,{"derivedFrom":[subQ7,subQ6]}),subQ4]})]});}
            var Q23;
            {var subQ0=sQuery(id+"F8.wireOp",EDGE,"E72");var subQ1=sQuery(id+"F8.wireOp",EDGE,"E71");var subQ2=sQuery(id+"F8.wireOp",EDGE,"E70");var subQ3=sQuery(id+"F8.wireOp",EDGE,"E69.1");var subQ4=makeQuery(id+"F18.opExtrude","CAP_FACE",FACE,{"disambiguationData":[OSD([subQ3,subQ2,subQ1,subQ0,sQuery(id+"F8.wireOp",EDGE,"E75")])],"isStart":false});var subQ5=sQuery(id+"F7.wireOp",EDGE,"E59");var subQ6=makeQuery(id+"F17.opExtrude","SWEPT_FACE",FACE,{"disambiguationData":[OSD([subQ5])]});var subQ7=makeQuery(id+"F16.opExtrude","SWEPT_FACE",FACE,{"disambiguationData":[OSD([subQ5])]});Q23=makeQuery(id+"F21.opChamfer","BLEND_EDGE",EDGE,{"blendedFrom":[makeQuery(id+"F20.boolean.opBoolean","SPLIT",EDGE,{"disambiguationData":[TD([subQ7])],"derivedFrom":makeQuery(id+"F18.opExtrude","SWEPT_EDGE",EDGE,{"disambiguationData":[OSD([subQ2,subQ0])]})}),makeQuery(id+"F18.boolean.opBoolean","MERGE",FACE,{"derivedFrom":[makeQuery(id+"F17.boolean.opBoolean","MERGE",FACE,{"derivedFrom":[subQ7,subQ6]}),subQ4]})],"blendedInto":[makeQuery(id+"F18.boolean.opBoolean","MERGE",FACE,{"derivedFrom":[makeQuery(id+"F17.boolean.opBoolean","MERGE",FACE,{"derivedFrom":[subQ7,subQ6]}),subQ4]})]});}
            var Q24;
            Q24=makeQuery(id+"F18.opExtrude","CAP_EDGE",EDGE,{"disambiguationData":[OSD([sQuery(id+"F8.wireOp",EDGE,"E70")])],"isStart":false});
            var Q25;
            {var subQ0=sQuery(id+"F8.wireOp",EDGE,"E72");var subQ1=sQuery(id+"F8.wireOp",EDGE,"E71");var subQ2=sQuery(id+"F8.wireOp",EDGE,"E70");var subQ3=sQuery(id+"F8.wireOp",EDGE,"E69.1");var subQ4=makeQuery(id+"F18.opExtrude","CAP_FACE",FACE,{"disambiguationData":[OSD([subQ3,subQ2,subQ1,subQ0,sQuery(id+"F8.wireOp",EDGE,"E75")])],"isStart":false});var subQ5=sQuery(id+"F7.wireOp",EDGE,"E59");var subQ6=makeQuery(id+"F17.opExtrude","SWEPT_FACE",FACE,{"disambiguationData":[OSD([subQ5])]});var subQ7=makeQuery(id+"F16.opExtrude","SWEPT_FACE",FACE,{"disambiguationData":[OSD([subQ5])]});Q25=makeQuery(id+"F21.opChamfer","BLEND_EDGE",EDGE,{"blendedFrom":[makeQuery(id+"F20.boolean.opBoolean","SPLIT",EDGE,{"disambiguationData":[TD([subQ7])],"derivedFrom":makeQuery(id+"F18.opExtrude","SWEPT_EDGE",EDGE,{"disambiguationData":[OSD([subQ2,subQ1])]})}),makeQuery(id+"F18.boolean.opBoolean","MERGE",FACE,{"derivedFrom":[makeQuery(id+"F17.boolean.opBoolean","MERGE",FACE,{"derivedFrom":[subQ7,subQ6]}),subQ4]})],"blendedInto":[makeQuery(id+"F18.boolean.opBoolean","MERGE",FACE,{"derivedFrom":[makeQuery(id+"F17.boolean.opBoolean","MERGE",FACE,{"derivedFrom":[subQ7,subQ6]}),subQ4]})]});}
            fillet(context, id + "F22", {"entities" : qUnion([Q0, Q1, Q2, Q3, Q4, Q5, Q6, Q7, Q8, Q9, Q10, Q11, Q12, Q13, Q14, Q15, Q16, Q17, Q18, Q19, Q20, Q21, Q22, Q23, Q24, Q25]), "radius" : 1.5 * mm, "tangentPropagation" : true, "allowEdgeOverflow" : false});
        }
        {
            var Q0;
            Q0=makeQuery(id+"F17.opExtrude","SWEPT_EDGE",EDGE,{"disambiguationData":[OSD([sQuery(id+"F7.wireOp",EDGE,"E47"),sQuery(id+"F7.wireOp",EDGE,"E54")])]});
            var Q1;
            Q1=makeQuery(id+"F17.opExtrude","SWEPT_EDGE",EDGE,{"disambiguationData":[OSD([sQuery(id+"F7.wireOp",EDGE,"E48"),sQuery(id+"F7.wireOp",EDGE,"E51")])]});
            var Q2;
            Q2=makeQuery(id+"F17.opExtrude","SWEPT_EDGE",EDGE,{"disambiguationData":[OSD([sQuery(id+"F7.wireOp",EDGE,"E39"),sQuery(id+"F7.wireOp",EDGE,"E62")])]});
            var Q3;
            Q3=makeQuery(id+"F17.opExtrude","SWEPT_EDGE",EDGE,{"disambiguationData":[OSD([sQuery(id+"F7.wireOp",EDGE,"E42"),sQuery(id+"F7.wireOp",EDGE,"E62")])]});
            var Q4;
            Q4=makeQuery(id+"F17.opExtrude","SWEPT_EDGE",EDGE,{"disambiguationData":[OSD([sQuery(id+"F7.wireOp",EDGE,"E45"),sQuery(id+"F7.wireOp",EDGE,"E52")])]});
            var Q5;
            Q5=makeQuery(id+"F17.opExtrude","SWEPT_EDGE",EDGE,{"disambiguationData":[OSD([sQuery(id+"F7.wireOp",EDGE,"E46"),sQuery(id+"F7.wireOp",EDGE,"E53")])]});
            var Q6;
            Q6=makeQuery(id+"F17.opExtrude","SWEPT_EDGE",EDGE,{"disambiguationData":[OSD([sQuery(id+"F7.wireOp",EDGE,"E50"),sQuery(id+"F7.wireOp",EDGE,"E59")])]});
            var Q7;
            Q7=makeQuery(id+"F17.opExtrude","SWEPT_EDGE",EDGE,{"disambiguationData":[OSD([sQuery(id+"F7.wireOp",EDGE,"E49"),sQuery(id+"F7.wireOp",EDGE,"E59")])]});
            var Q8;
            Q8=makeQuery(id+"F17.opExtrude","SWEPT_EDGE",EDGE,{"disambiguationData":[OSD([sQuery(id+"F7.wireOp",EDGE,"E50"),sQuery(id+"F7.wireOp",EDGE,"E53")])]});
            var Q9;
            Q9=makeQuery(id+"F17.opExtrude","SWEPT_EDGE",EDGE,{"disambiguationData":[OSD([sQuery(id+"F7.wireOp",EDGE,"E49"),sQuery(id+"F7.wireOp",EDGE,"E52")])]});
            var Q10;
            Q10=makeQuery(id+"F17.opExtrude","SWEPT_EDGE",EDGE,{"disambiguationData":[OSD([sQuery(id+"F7.wireOp",EDGE,"E39"),sQuery(id+"F7.wireOp",EDGE,"E51")])]});
            var Q11;
            Q11=makeQuery(id+"F17.opExtrude","SWEPT_EDGE",EDGE,{"disambiguationData":[OSD([sQuery(id+"F7.wireOp",EDGE,"E42"),sQuery(id+"F7.wireOp",EDGE,"E54")])]});
            var Q12;
            Q12=makeQuery(id+"F17.opExtrude","CAP_EDGE",EDGE,{"disambiguationData":[OSD([sQuery(id+"F7.wireOp",EDGE,"E57")])],"isStart":true});
            var Q13;
            Q13=makeQuery(id+"F17.opExtrude","CAP_EDGE",EDGE,{"disambiguationData":[OSD([sQuery(id+"F7.wireOp",EDGE,"E55")])],"isStart":true});
            fillet(context, id + "F23", {"entities" : qUnion([Q0, Q1, Q2, Q3, Q4, Q5, Q6, Q7, Q8, Q9, Q10, Q11, Q12, Q13]), "radius" : 0.5 * mm, "tangentPropagation" : true, "allowEdgeOverflow" : false});
        }
        {
            var Q0;
            Q0=makeQuery(id+"F9.opExtrude","SWEPT_EDGE",EDGE,{"disambiguationData":[OSD([sQuery(id+"F4.wireOp",EDGE,"E13.top"),sQuery(id+"F4.wireOp",EDGE,"E13.left")])]});
            fillet(context, id + "F24", {"entities" : qUnion([Q0]), "radius" : 5 * mm, "tangentPropagation" : true, "allowEdgeOverflow" : false});
        }
    });
